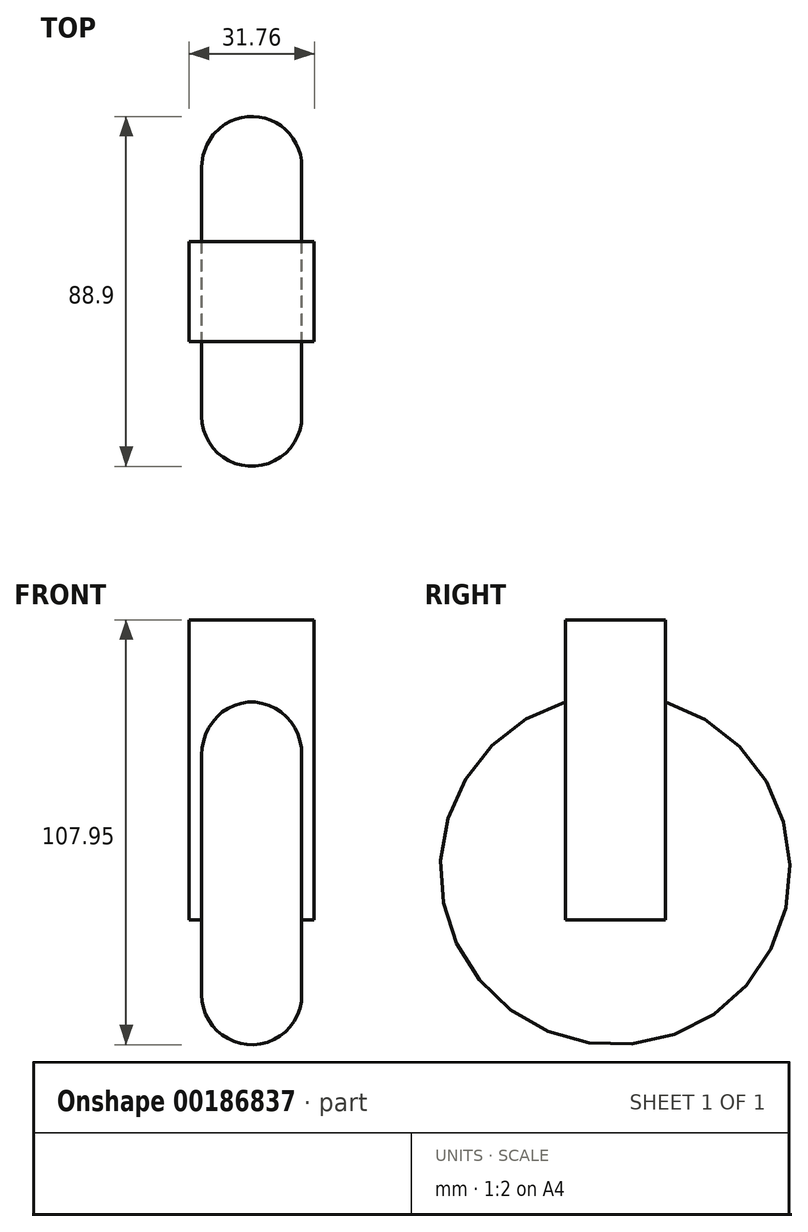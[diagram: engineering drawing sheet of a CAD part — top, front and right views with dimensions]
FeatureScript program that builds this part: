
annotation { "Feature Type Name" : "Feature", "Feature Type Description" : "" }
export const myFeature = defineFeature(function(context is Context, id is Id, definition is map)
    precondition{}
    {
        {
            var Q0;
            Q0=qCreatedBy(makeId("Right.planeOp"),FACE);
            var sketch = newSketch(context, id + "F0", { "sketchPlane" : qUnion([Q0])});
            skCircle(sketch, "E0", {"center": v(0, 0) * mm, "radius": 44.45 * mm});
            skCircle(sketch, "E1", {"center": v(0, 0) * mm, "radius": 6.35 * mm});
            skSolve(sketch);
        }
        {
            var Q0;
            Q0 = qSketchRegion(id + "F0", true);
            extrude(context, id + "F1", {"entities" : qUnion([Q0]), "endBound" : BoundingType.SYMMETRIC, "depth" : 25.4 * mm});
        }
        {
            var Q0;
            Q0=makeQuery(id+"F1.opExtrude","CAP_EDGE",EDGE,{"disambiguationData":[OSD([sQuery(id+"F0.wireOp",EDGE,"E0")])],"isStart":false});
            var Q1;
            Q1=makeQuery(id+"F1.opExtrude","CAP_EDGE",EDGE,{"disambiguationData":[OSD([sQuery(id+"F0.wireOp",EDGE,"E0")])],"isStart":true});
            fillet(context, id + "F2", {"entities" : qUnion([Q0, Q1]), "radius" : 12.7 * mm, "tangentPropagation" : true, "allowEdgeOverflow" : false});
        }
        {
            var Q0;
            Q0=qCreatedBy(makeId("Front.planeOp"),FACE);
            var sketch = newSketch(context, id + "F3", { "sketchPlane" : qUnion([Q0])});
            skLineSegment(sketch, "E2.bottom", {"start": v(-15.87, 63.5) * mm, "end": v(15.88, 63.5) * mm});
            skLineSegment(sketch, "E2.left", {"start": v(-15.87, 63.5) * mm, "end": v(-15.88, -12.7) * mm});
            skLineSegment(sketch, "E2.right", {"start": v(15.88, 63.5) * mm, "end": v(15.87, -12.7) * mm});
            skPoint(sketch, "E2.middle", {"position": v(0, 0) * mm});
            skLineSegment(sketch, "E3.bottom", {"start": v(-15.88, -12.7) * mm, "end": v(15.88, -12.7) * mm});
            skLineSegment(sketch, "E3.left", {"start": v(-15.88, -12.7) * mm, "end": v(-15.88, 12.7) * mm});
            skLineSegment(sketch, "E3.right", {"start": v(15.88, -12.7) * mm, "end": v(15.88, 12.7) * mm});
            skSolve(sketch);
        }
        {
            var Q0;
            Q0 = qSketchRegion(id + "F3", true);
            extrude(context, id + "F4", {"entities" : qUnion([Q0]), "operationType" : NewBodyOperationType.ADD, "endBound" : BoundingType.SYMMETRIC, "depth" : 25.4 * mm});
        }
    });
